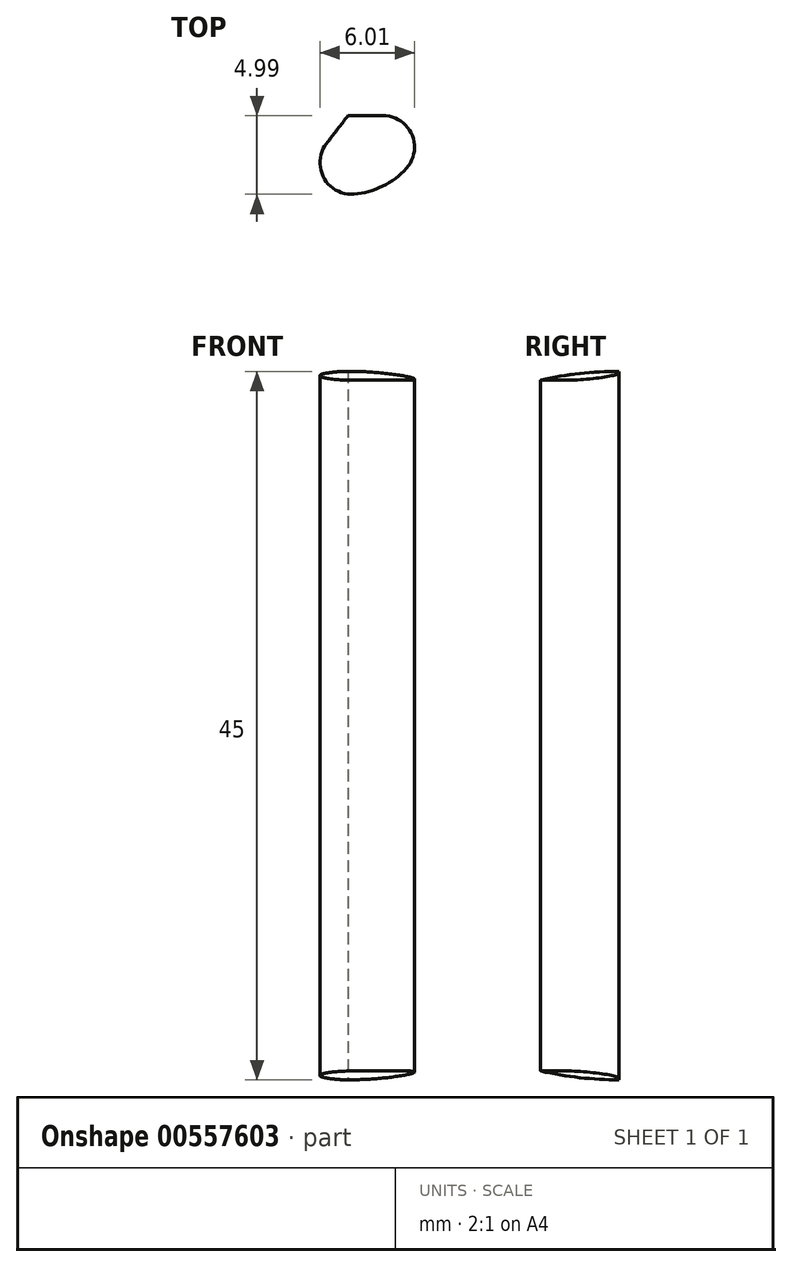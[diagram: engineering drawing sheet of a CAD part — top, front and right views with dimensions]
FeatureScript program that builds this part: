
annotation { "Feature Type Name" : "Feature", "Feature Type Description" : "" }
export const myFeature = defineFeature(function(context is Context, id is Id, definition is map)
    precondition{}
    {
        {
            var Q0;
            Q0=qCreatedBy(makeId("Front.planeOp"),FACE);
            var sketch = newSketch(context, id + "F0", { "sketchPlane" : qUnion([Q0])});
            skPoint(sketch, "E0.middle", {"position": v(0, 0) * mm});
            skCircle(sketch, "E1", {"center": v(0, 0) * mm, "radius": 22.5 * mm});
            skLineSegment(sketch, "E2", {"start": v(0, 22.5) * mm, "end": v(0, -22.5) * mm});
            skCircle(sketch, "E3", {"center": v(0, 0) * mm, "radius": 17.13 * mm});
            skLineSegment(sketch, "E4", {"start": v(5, -23.88) * mm, "end": v(5, 25.4) * mm});
            skSolve(sketch);
        }
        {
            var Q0;
            {var subQ0=sQuery(id+"F0.wireOp",EDGE,"E2");Q0=makeQuery(id+"F0.imprint","IMPRINT",FACE,{"disambiguationData":[TD([[makeQuery(id+"F0.imprint","IMPRINT",EDGE,{"derivedFrom":subQ0}),1.0]])]});}
            var Q1;
            {var subQ0=sQuery(id+"F0.wireOp",EDGE,"E4");var subQ1=sQuery(id+"F0.wireOp",EDGE,"E1");var subQ2=makeQuery(id+"F0.imprint","INTERSECT",VERTEX,{"disambiguationData":[OD(0.0)],"derivedFrom":[subQ1,subQ0]});Q1=makeQuery(id+"F0.imprint","IMPRINT",FACE,{"disambiguationData":[TD([[makeQuery(id+"F0.imprint","IMPRINT",EDGE,{"disambiguationData":[TD([[subQ2,1.0]])],"derivedFrom":subQ1}),1.0]])]});}
            var Q2;
            Q2=sQuery(id+"F0.wireOp",EDGE,"E2");
            revolve(context, id + "F1", {"entities" : qUnion([Q0, Q1]), "axis" : qUnion([Q2]), "revolveType" : RevolveType.ONE_DIRECTION, "angle" : 127.64 * degree});
        }
        {
            var Q0;
            Q0=makeQuery(id+"F1.opRevolve","CAP_EDGE",EDGE,{"disambiguationData":[OSD([sQuery(id+"F0.wireOp",EDGE,"E4")])],"isStart":false});
            var Q1;
            Q1=makeQuery(id+"F1.opRevolve","CAP_EDGE",EDGE,{"disambiguationData":[OSD([sQuery(id+"F0.wireOp",EDGE,"E4")])],"isStart":true});
            fillet(context, id + "F2", {"entities" : qUnion([Q0, Q1]), "radius" : 2 * mm, "tangentPropagation" : true, "allowEdgeOverflow" : false});
        }
    });
